# Revit family: Furniture-Floor_Mount-Vanity-KOHLER-Charlemont-K-29261-1
name_source: partatom
category: Plumbing Fixtures
units: mm (PartAtom-declared; Revit-internal decimal feet)

## family parameters
Cut with Voids When Loaded = No
Host = Face
Maintain Annotation Orientation = No
OmniClass Number = 23.31.13.00
Part Type = Normal
Room Calculation Point = No
Round Connector Dimension = Use Diameter
Shared = No

## types (5) — shared parameters
ADA Compliant = No
Assembly Code = D2010400
CW Connection = No
Cold Water Inlet = Cold Water Inlet
Date Modified = 03/06/2025
Default Elevation = 0"
Description = 36 inch bathroom vanity cabinet with sink and quartz top
Drain Included = No
HW Connection = No
Height = 39 11/16"
Hot Water Inlet = Hot Water Inlet
Length = 22 7/16"
Manufacturer = Kohler Co.
Master Format 2014 = 22 41 16
Master Format 2014 Name = Residential Lavatories and Sinks
Material = Solid Wood Construction
Product Documentation Link = https://www.us.kohler.com
Product Name = Charlemont
Product Page URL = http://www.us.kohler.com
URL = https://www.us.kohler.com
Vent Connection = No
Waste Connection = Yes
Waste Water Outlet = Waste Water Outlet
WaterSense Certified = No
Width = 36 15/16"

## per-type parameters (varying)
| type | Finish | Model | Secondary Finish | Type |
| 0-White | Kohler-Wood-Molded-0-White | K-29261-BD1-0 | Kohler-Metal-BN-Vibrant_Brushed_Nickel | 1 |
| DWG-Warm Dark Grey | KOHLER-Wood-DWG-Warm_Dark_Grey | K-29261-BD1-DWG | Kohler-Metal-2MB-Vibrant_Brushed_Moderne_Brass | 2 |
| WEK-Weathered Oak | KOHLER-Wood-WEK-Weathered_Oak | K-29261-BD1-WEK | Kohler-Metal-BL-Matte_Black | 3 |
| TDB-Tidal Blue | KOHLER-Wood-TDB-Tidal_Blue | K-29261-BD1-TDB | Kohler-Metal-2MB-Vibrant_Brushed_Moderne_Brass | 4 |
| DAK-Draper Oak | KOHLER-Wood-DAK-Draper_Oak | K-29261-BD1-0 | Kohler-Metal-BN-Vibrant_Brushed_Nickel | 1 |

## geometry (parser evidence)
native form markers: Sweep x5
no freeform markers — native parametric forms only
